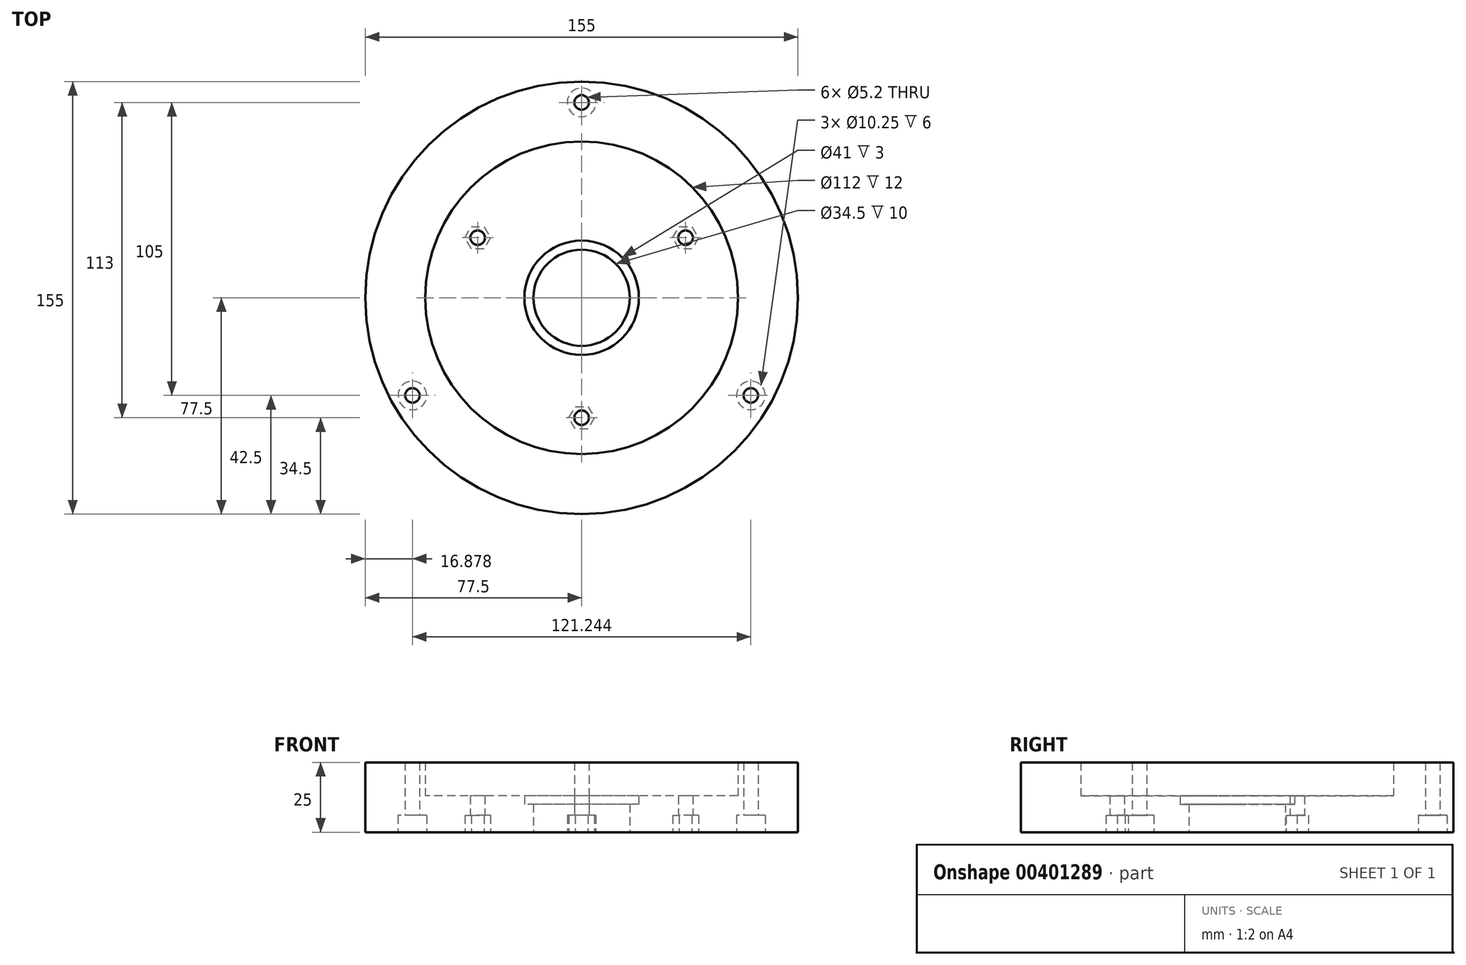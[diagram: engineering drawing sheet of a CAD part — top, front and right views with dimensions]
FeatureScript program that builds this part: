
annotation { "Feature Type Name" : "Feature", "Feature Type Description" : "" }
export const myFeature = defineFeature(function(context is Context, id is Id, definition is map)
    precondition{}
    {
        {
            var Q0;
            Q0=qCreatedBy(makeId("Top.planeOp"),FACE);
            var sketch = newSketch(context, id + "F0", { "sketchPlane" : qUnion([Q0])});
            skCircle(sketch, "E0", {"center": v(0, 0) * mm, "radius": 77.5 * mm});
            skCircle(sketch, "E1", {"center": v(0, 0) * mm, "radius": 56 * mm});
            skLineSegment(sketch, "E2", {"start": v(0, 0) * mm, "end": v(75.77, 43.75) * mm, "construction": true});
            skCircle(sketch, "E3", {"center": v(37.24, 21.5) * mm, "radius": 2.6 * mm});
            skCircle(sketch, "E4", {"center": v(0, 0) * mm, "radius": 20.5 * mm});
            skCircle(sketch, "E5", {"center": v(0, 0) * mm, "radius": 17.25 * mm});
            skCircle(sketch, "E6", {"center": v(0, 70) * mm, "radius": 2.6 * mm});
            skCircle(sketch, "E7", {"center": v(0, 70) * mm, "radius": 5.12 * mm});
            skCircle(sketch, "E8.1.0", {"center": v(-60.62, -35) * mm, "radius": 5.12 * mm});
            skCircle(sketch, "E8.1.1", {"center": v(-60.62, -35) * mm, "radius": 2.6 * mm});
            skCircle(sketch, "E8.2.0", {"center": v(60.62, -35) * mm, "radius": 5.12 * mm});
            skCircle(sketch, "E8.2.1", {"center": v(60.62, -35) * mm, "radius": 2.6 * mm});
            skCircle(sketch, "E9.cCircle", {"center": v(37.24, 21.5) * mm, "radius": 4.6 * mm, "construction": true});
            skLineSegment(sketch, "E9.0", {"start": v(32.64, 21.5) * mm, "end": v(34.94, 25.48) * mm});
            skLineSegment(sketch, "E9.1", {"start": v(34.94, 25.48) * mm, "end": v(39.54, 25.48) * mm});
            skLineSegment(sketch, "E9.2", {"start": v(39.54, 25.48) * mm, "end": v(41.84, 21.5) * mm});
            skLineSegment(sketch, "E9.3", {"start": v(41.84, 21.5) * mm, "end": v(39.54, 17.52) * mm});
            skLineSegment(sketch, "E9.4", {"start": v(39.54, 17.52) * mm, "end": v(34.94, 17.52) * mm});
            skLineSegment(sketch, "E9.5", {"start": v(34.94, 17.52) * mm, "end": v(32.64, 21.5) * mm});
            skLineSegment(sketch, "E10.1.0", {"start": v(-32.64, 21.5) * mm, "end": v(-34.94, 17.52) * mm});
            skLineSegment(sketch, "E10.1.1", {"start": v(-39.54, 25.48) * mm, "end": v(-34.94, 25.48) * mm});
            skLineSegment(sketch, "E10.1.2", {"start": v(-34.94, 25.48) * mm, "end": v(-32.64, 21.5) * mm});
            skCircle(sketch, "E10.1.3", {"center": v(-37.24, 21.5) * mm, "radius": 2.6 * mm});
            skLineSegment(sketch, "E10.1.4", {"start": v(-39.54, 17.52) * mm, "end": v(-41.84, 21.5) * mm});
            skCircle(sketch, "E10.1.5", {"center": v(-37.24, 21.5) * mm, "radius": 4.6 * mm, "construction": true});
            skLineSegment(sketch, "E10.1.6", {"start": v(-41.84, 21.5) * mm, "end": v(-39.54, 25.48) * mm});
            skLineSegment(sketch, "E10.1.7", {"start": v(-34.94, 17.52) * mm, "end": v(-39.54, 17.52) * mm});
            skLineSegment(sketch, "E10.2.0", {"start": v(-2.3, -39.02) * mm, "end": v(2.3, -39.02) * mm});
            skLineSegment(sketch, "E10.2.1", {"start": v(-2.3, -46.98) * mm, "end": v(-4.6, -43) * mm});
            skLineSegment(sketch, "E10.2.2", {"start": v(-4.6, -43) * mm, "end": v(-2.3, -39.02) * mm});
            skCircle(sketch, "E10.2.3", {"center": v(0, -43) * mm, "radius": 2.6 * mm});
            skLineSegment(sketch, "E10.2.4", {"start": v(4.6, -43) * mm, "end": v(2.3, -46.98) * mm});
            skCircle(sketch, "E10.2.5", {"center": v(0, -43) * mm, "radius": 4.6 * mm, "construction": true});
            skLineSegment(sketch, "E10.2.6", {"start": v(2.3, -46.98) * mm, "end": v(-2.3, -46.98) * mm});
            skLineSegment(sketch, "E10.2.7", {"start": v(2.3, -39.02) * mm, "end": v(4.6, -43) * mm});
            skSolve(sketch);
        }
        {
            var Q0;
            Q0=makeQuery(id+"F0.imprint","IMPRINT",FACE,{"disambiguationData":[TD([[makeQuery(id+"F0.imprint","IMPRINT",EDGE,{"derivedFrom":sQuery(id+"F0.wireOp",EDGE,"E0")}),1.0]])]});
            var Q1;
            Q1=makeQuery(id+"F0.imprint","IMPRINT",FACE,{"disambiguationData":[TD([[makeQuery(id+"F0.imprint","IMPRINT",EDGE,{"derivedFrom":sQuery(id+"F0.wireOp",EDGE,"E1")}),1.0]])]});
            var Q2;
            Q2=makeQuery(id+"F0.imprint","IMPRINT",FACE,{"disambiguationData":[TD([[makeQuery(id+"F0.imprint","IMPRINT",EDGE,{"derivedFrom":sQuery(id+"F0.wireOp",EDGE,"E6")}),-1.0]])]});
            var Q3;
            Q3=makeQuery(id+"F0.imprint","IMPRINT",FACE,{"disambiguationData":[TD([[makeQuery(id+"F0.imprint","IMPRINT",EDGE,{"derivedFrom":sQuery(id+"F0.wireOp",EDGE,"E10.1.0")}),-1.0]])]});
            var Q4;
            Q4=makeQuery(id+"F0.imprint","IMPRINT",FACE,{"disambiguationData":[TD([[makeQuery(id+"F0.imprint","IMPRINT",EDGE,{"derivedFrom":sQuery(id+"F0.wireOp",EDGE,"E3")}),-1.0]])]});
            var Q5;
            Q5=makeQuery(id+"F0.imprint","IMPRINT",FACE,{"disambiguationData":[TD([[makeQuery(id+"F0.imprint","IMPRINT",EDGE,{"derivedFrom":sQuery(id+"F0.wireOp",EDGE,"E8.2.0")}),1.0]])]});
            var Q6;
            Q6=makeQuery(id+"F0.imprint","IMPRINT",FACE,{"disambiguationData":[TD([[makeQuery(id+"F0.imprint","IMPRINT",EDGE,{"derivedFrom":sQuery(id+"F0.wireOp",EDGE,"E10.2.0")}),-1.0]])]});
            var Q7;
            Q7=makeQuery(id+"F0.imprint","IMPRINT",FACE,{"disambiguationData":[TD([[makeQuery(id+"F0.imprint","IMPRINT",EDGE,{"derivedFrom":sQuery(id+"F0.wireOp",EDGE,"E8.1.0")}),1.0]])]});
            extrude(context, id + "F1", {"entities" : qUnion([Q0, Q1, Q2, Q3, Q4, Q5, Q6, Q7]), "depth" : 13 * mm, "offsetDistance" : 25 * mm});
        }
        {
            var Q0;
            Q0=makeQuery(id+"F0.imprint","IMPRINT",FACE,{"disambiguationData":[TD([[makeQuery(id+"F0.imprint","IMPRINT",EDGE,{"derivedFrom":sQuery(id+"F0.wireOp",EDGE,"E0")}),1.0]])]});
            var Q1;
            Q1=makeQuery(id+"F0.imprint","IMPRINT",FACE,{"disambiguationData":[TD([[makeQuery(id+"F0.imprint","IMPRINT",EDGE,{"derivedFrom":sQuery(id+"F0.wireOp",EDGE,"E6")}),-1.0]])]});
            var Q2;
            Q2=makeQuery(id+"F0.imprint","IMPRINT",FACE,{"disambiguationData":[TD([[makeQuery(id+"F0.imprint","IMPRINT",EDGE,{"derivedFrom":sQuery(id+"F0.wireOp",EDGE,"E8.2.0")}),1.0]])]});
            var Q3;
            Q3=makeQuery(id+"F0.imprint","IMPRINT",FACE,{"disambiguationData":[TD([[makeQuery(id+"F0.imprint","IMPRINT",EDGE,{"derivedFrom":sQuery(id+"F0.wireOp",EDGE,"E8.1.0")}),1.0]])]});
            extrude(context, id + "F2", {"entities" : qUnion([Q0, Q1, Q2, Q3]), "operationType" : NewBodyOperationType.ADD, "depth" : 25 * mm, "offsetDistance" : 25 * mm});
        }
        {
            var Q0;
            Q0=makeQuery(id+"F0.imprint","IMPRINT",FACE,{"disambiguationData":[TD([[makeQuery(id+"F0.imprint","IMPRINT",EDGE,{"derivedFrom":sQuery(id+"F0.wireOp",EDGE,"E4")}),1.0]])]});
            extrude(context, id + "F3", {"entities" : qUnion([Q0]), "operationType" : NewBodyOperationType.ADD, "depth" : 10 * mm, "offsetDistance" : 25 * mm});
        }
        {
            var Q0;
            Q0=makeQuery(id+"F0.imprint","IMPRINT",FACE,{"disambiguationData":[TD([[makeQuery(id+"F0.imprint","IMPRINT",EDGE,{"derivedFrom":sQuery(id+"F0.wireOp",EDGE,"E6")}),-1.0]])]});
            var Q1;
            Q1=makeQuery(id+"F0.imprint","IMPRINT",FACE,{"disambiguationData":[TD([[makeQuery(id+"F0.imprint","IMPRINT",EDGE,{"derivedFrom":sQuery(id+"F0.wireOp",EDGE,"E8.1.0")}),1.0]])]});
            var Q2;
            Q2=makeQuery(id+"F0.imprint","IMPRINT",FACE,{"disambiguationData":[TD([[makeQuery(id+"F0.imprint","IMPRINT",EDGE,{"derivedFrom":sQuery(id+"F0.wireOp",EDGE,"E8.2.0")}),1.0]])]});
            extrude(context, id + "F4", {"entities" : qUnion([Q0, Q1, Q2]), "operationType" : NewBodyOperationType.REMOVE, "depth" : 6 * mm, "offsetDistance" : 25 * mm});
        }
        {
            var Q0;
            Q0=makeQuery(id+"F0.imprint","IMPRINT",FACE,{"disambiguationData":[TD([[makeQuery(id+"F0.imprint","IMPRINT",EDGE,{"derivedFrom":sQuery(id+"F0.wireOp",EDGE,"E3")}),-1.0]])]});
            var Q1;
            Q1=makeQuery(id+"F0.imprint","IMPRINT",FACE,{"disambiguationData":[TD([[makeQuery(id+"F0.imprint","IMPRINT",EDGE,{"derivedFrom":sQuery(id+"F0.wireOp",EDGE,"E10.1.0")}),-1.0]])]});
            var Q2;
            Q2=makeQuery(id+"F0.imprint","IMPRINT",FACE,{"disambiguationData":[TD([[makeQuery(id+"F0.imprint","IMPRINT",EDGE,{"derivedFrom":sQuery(id+"F0.wireOp",EDGE,"E10.2.0")}),-1.0]])]});
            extrude(context, id + "F5", {"entities" : qUnion([Q0, Q1, Q2]), "operationType" : NewBodyOperationType.REMOVE, "depth" : 6 * mm, "offsetDistance" : 25 * mm});
        }
    });
